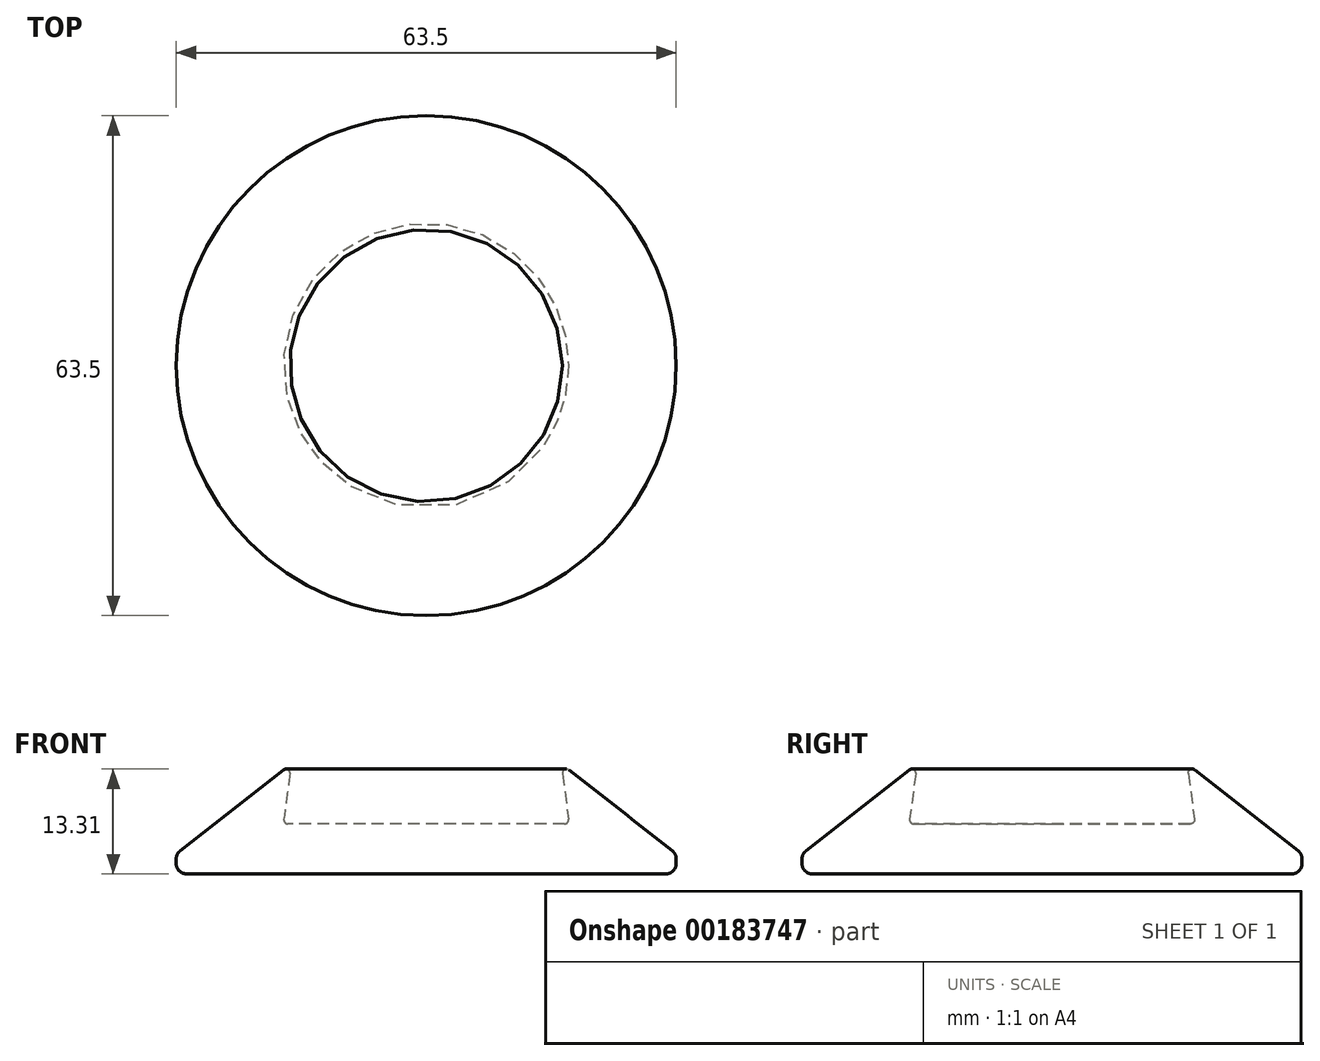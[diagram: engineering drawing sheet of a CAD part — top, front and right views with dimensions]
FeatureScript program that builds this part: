
annotation { "Feature Type Name" : "Feature", "Feature Type Description" : "" }
export const myFeature = defineFeature(function(context is Context, id is Id, definition is map)
    precondition{}
    {
        {
            var Q0;
            Q0=qCreatedBy(makeId("Front.planeOp"),FACE);
            var sketch = newSketch(context, id + "F0", { "sketchPlane" : qUnion([Q0])});
            skLineSegment(sketch, "E0", {"start": v(0, 0) * mm, "end": v(66.92, 0) * mm, "construction": true});
            skLineSegment(sketch, "E1", {"start": v(0, 0) * mm, "end": v(0, 49.99) * mm, "construction": true});
            skLineSegment(sketch, "E2", {"start": v(0, 0) * mm, "end": v(31.75, 0) * mm});
            skLineSegment(sketch, "E3", {"start": v(31.75, 0) * mm, "end": v(31.75, 2.54) * mm});
            skLineSegment(sketch, "E4", {"start": v(31.75, 2.54) * mm, "end": v(17.15, 13.97) * mm});
            skLineSegment(sketch, "E5", {"start": v(17.15, 13.97) * mm, "end": v(18.16, 6.35) * mm});
            skLineSegment(sketch, "E6", {"start": v(18.16, 6.35) * mm, "end": v(0, 6.35) * mm});
            skLineSegment(sketch, "E7", {"start": v(0, 6.35) * mm, "end": v(0, 0) * mm});
            skSolve(sketch);
        }
        {
            var Q0;
            Q0 = qSketchRegion(id + "F0", true);
            var Q1;
            Q1=sQuery(id+"F0.wireOp",EDGE,"E1");
            revolve(context, id + "F1", {"entities" : qUnion([Q0]), "axis" : qUnion([Q1]), "revolveType" : RevolveType.FULL});
        }
        {
            var Q0;
            Q0=makeQuery(id+"F1.opRevolve","SWEPT_FACE",FACE,{"disambiguationData":[OSD([sQuery(id+"F0.wireOp",EDGE,"E3")])]});
            fillet(context, id + "F2", {"entities" : qUnion([Q0]), "radius" : 1.27 * mm, "tangentPropagation" : true, "allowEdgeOverflow" : false});
        }
        {
            var Q0;
            Q0=makeQuery(id+"F1.opRevolve","SWEPT_FACE",FACE,{"disambiguationData":[OSD([sQuery(id+"F0.wireOp",EDGE,"E5")])]});
            fillet(context, id + "F3", {"entities" : qUnion([Q0]), "radius" : 0.5 * mm, "tangentPropagation" : true, "allowEdgeOverflow" : false});
        }
    });
